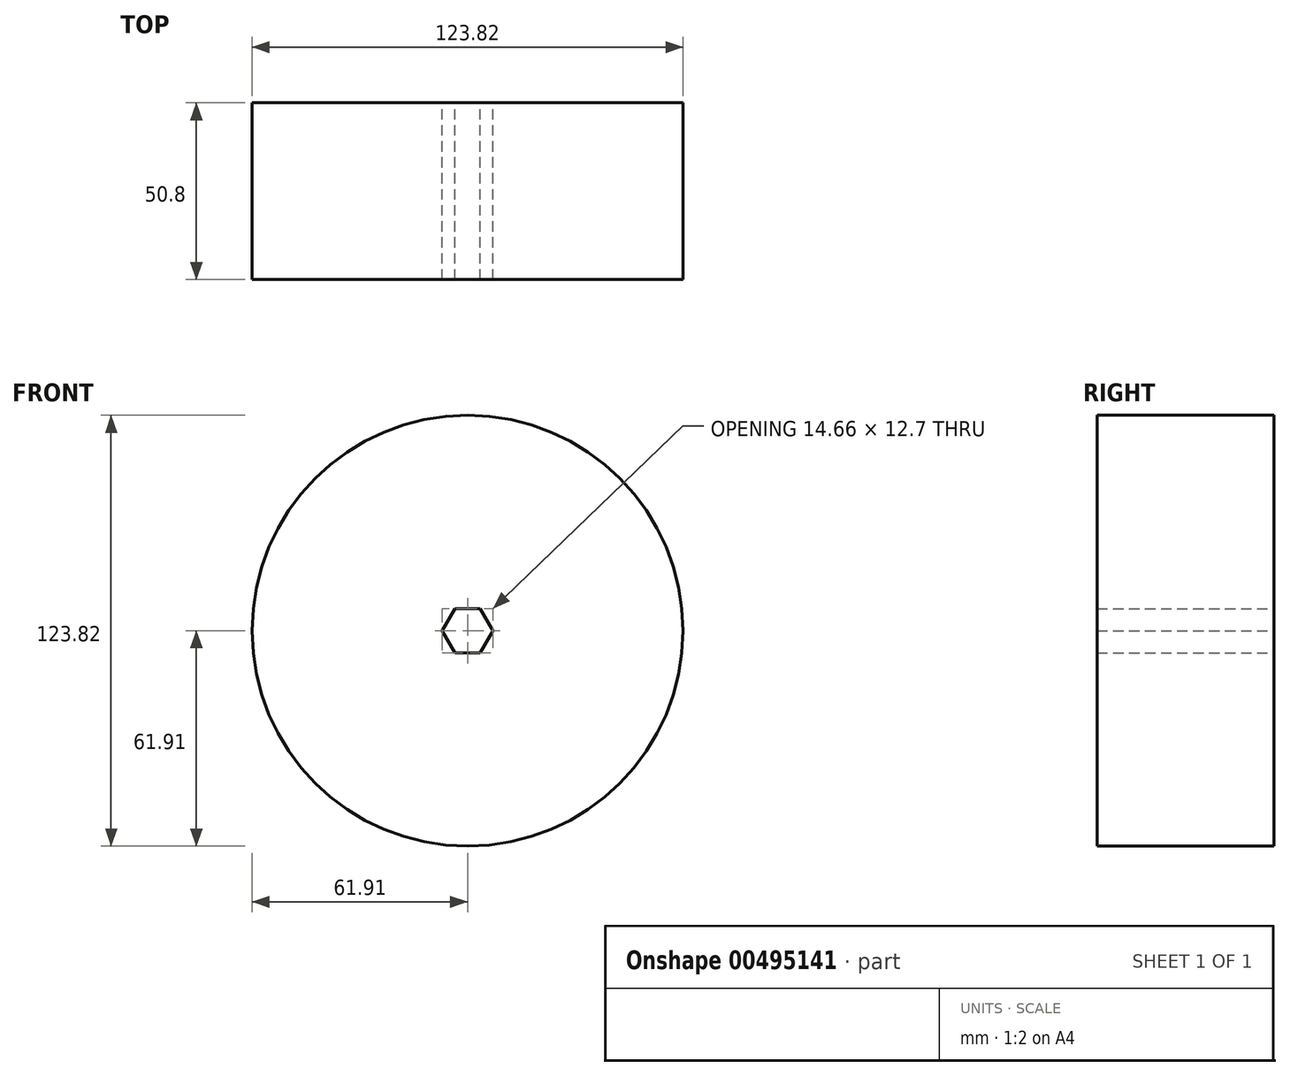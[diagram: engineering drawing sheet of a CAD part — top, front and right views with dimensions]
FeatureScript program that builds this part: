
annotation { "Feature Type Name" : "Feature", "Feature Type Description" : "" }
export const myFeature = defineFeature(function(context is Context, id is Id, definition is map)
    precondition{}
    {
        {
            var Q0;
            Q0=qCreatedBy(makeId("Front.planeOp"),FACE);
            var sketch = newSketch(context, id + "F0", { "sketchPlane" : qUnion([Q0])});
            skCircle(sketch, "E0", {"center": v(0, 0) * mm, "radius": 61.91 * mm});
            skCircle(sketch, "E1.cCircle", {"center": v(0, 0) * mm, "radius": 6.35 * mm, "construction": true});
            skLineSegment(sketch, "E1.0", {"start": v(-3.67, 6.35) * mm, "end": v(3.67, 6.35) * mm});
            skLineSegment(sketch, "E1.1", {"start": v(3.67, 6.35) * mm, "end": v(7.33, 0) * mm});
            skLineSegment(sketch, "E1.2", {"start": v(7.33, 0) * mm, "end": v(3.67, -6.35) * mm});
            skLineSegment(sketch, "E1.3", {"start": v(3.67, -6.35) * mm, "end": v(-3.67, -6.35) * mm});
            skLineSegment(sketch, "E1.4", {"start": v(-3.67, -6.35) * mm, "end": v(-7.33, 0) * mm});
            skLineSegment(sketch, "E1.5", {"start": v(-7.33, 0) * mm, "end": v(-3.67, 6.35) * mm});
            skPoint(sketch, "E1.0.midPoint", {"position": v(0, 6.35) * mm});
            skSolve(sketch);
        }
        {
            var Q0;
            Q0=qSketchRegion(id+"F0",true);
            extrude(context, id + "F1", {"entities" : qUnion([Q0]), "depth" : 50.8 * mm, "symmetric" : true});
        }
    });
